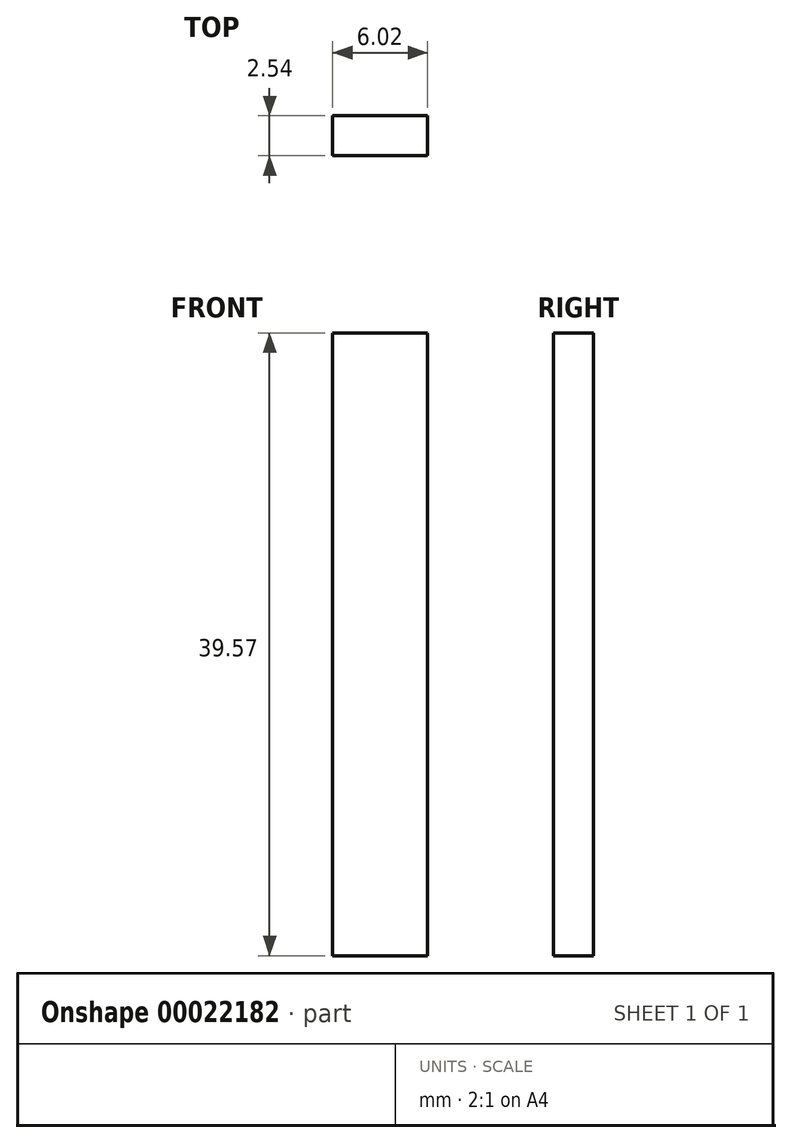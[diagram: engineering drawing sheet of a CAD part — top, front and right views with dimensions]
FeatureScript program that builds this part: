
annotation { "Feature Type Name" : "Feature", "Feature Type Description" : "" }
export const myFeature = defineFeature(function(context is Context, id is Id, definition is map)
    precondition{}
    {
        {
            var Q0;
            Q0=qCreatedBy(makeId("Front.planeOp"),FACE);
            var sketch = newSketch(context, id + "F0", { "sketchPlane" : qUnion([Q0])});
            skLineSegment(sketch, "E0", {"start": v(-50.76, 10.61) * mm, "end": v(-50.76, -28.96) * mm});
            skLineSegment(sketch, "E1", {"start": v(-50.76, -28.96) * mm, "end": v(-44.74, -28.96) * mm});
            skLineSegment(sketch, "E2", {"start": v(-44.74, -28.96) * mm, "end": v(-44.74, 10.61) * mm});
            skLineSegment(sketch, "E3", {"start": v(-50.76, 10.61) * mm, "end": v(-44.74, 10.61) * mm});
            skSolve(sketch);
        }
        {
            var Q0;
            Q0=makeQuery(id+"F0.imprint","IMPRINT",FACE,{"disambiguationData":[TD([[makeQuery(id+"F0.imprint","IMPRINT",EDGE,{"derivedFrom":sQuery(id+"F0.wireOp",EDGE,"E0")}),1.0]])]});
            extrude(context, id + "F1", {"entities" : qUnion([Q0]), "depth" : 2.54 * mm});
        }
    });
